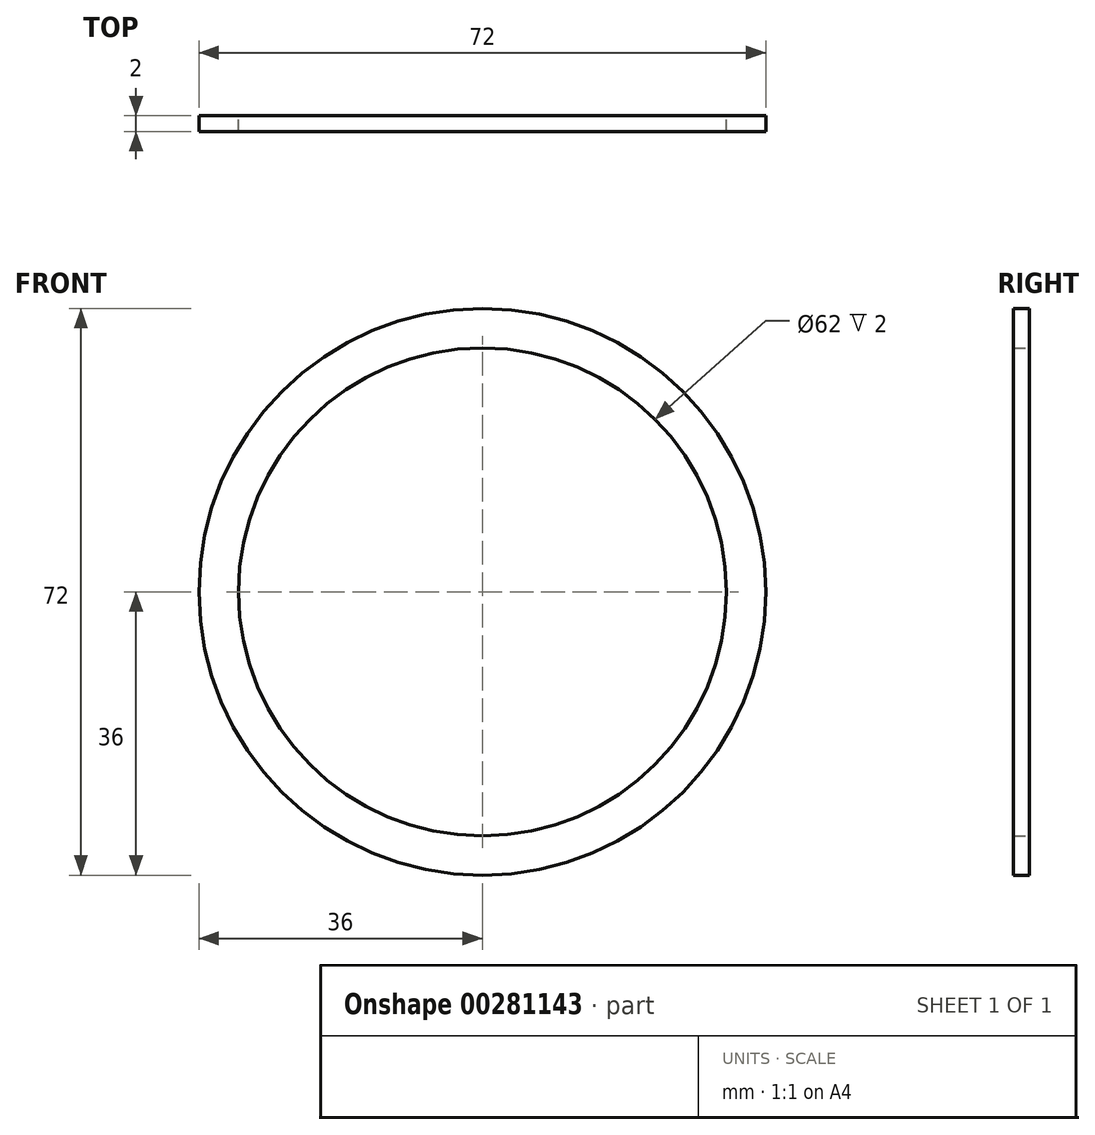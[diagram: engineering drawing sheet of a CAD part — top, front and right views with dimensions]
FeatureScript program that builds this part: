
annotation { "Feature Type Name" : "Feature", "Feature Type Description" : "" }
export const myFeature = defineFeature(function(context is Context, id is Id, definition is map)
    precondition{}
    {
        {
            var Q0;
            Q0=qCreatedBy(makeId("Front.planeOp"),FACE);
            var sketch = newSketch(context, id + "F0", { "sketchPlane" : qUnion([Q0])});
            skCircle(sketch, "E0", {"center": v(0, 0) * mm, "radius": 36 * mm});
            skCircle(sketch, "E1", {"center": v(0, 0) * mm, "radius": 31 * mm});
            skSolve(sketch);
        }
        {
            var Q0;
            Q0=makeQuery(id+"F0.imprint","IMPRINT",FACE,{"disambiguationData":[TD([[makeQuery(id+"F0.imprint","IMPRINT",EDGE,{"derivedFrom":sQuery(id+"F0.wireOp",EDGE,"E0")}),1.0]])]});
            extrude(context, id + "F1", {"entities" : qUnion([Q0]), "depth" : 2 * mm});
        }
    });
